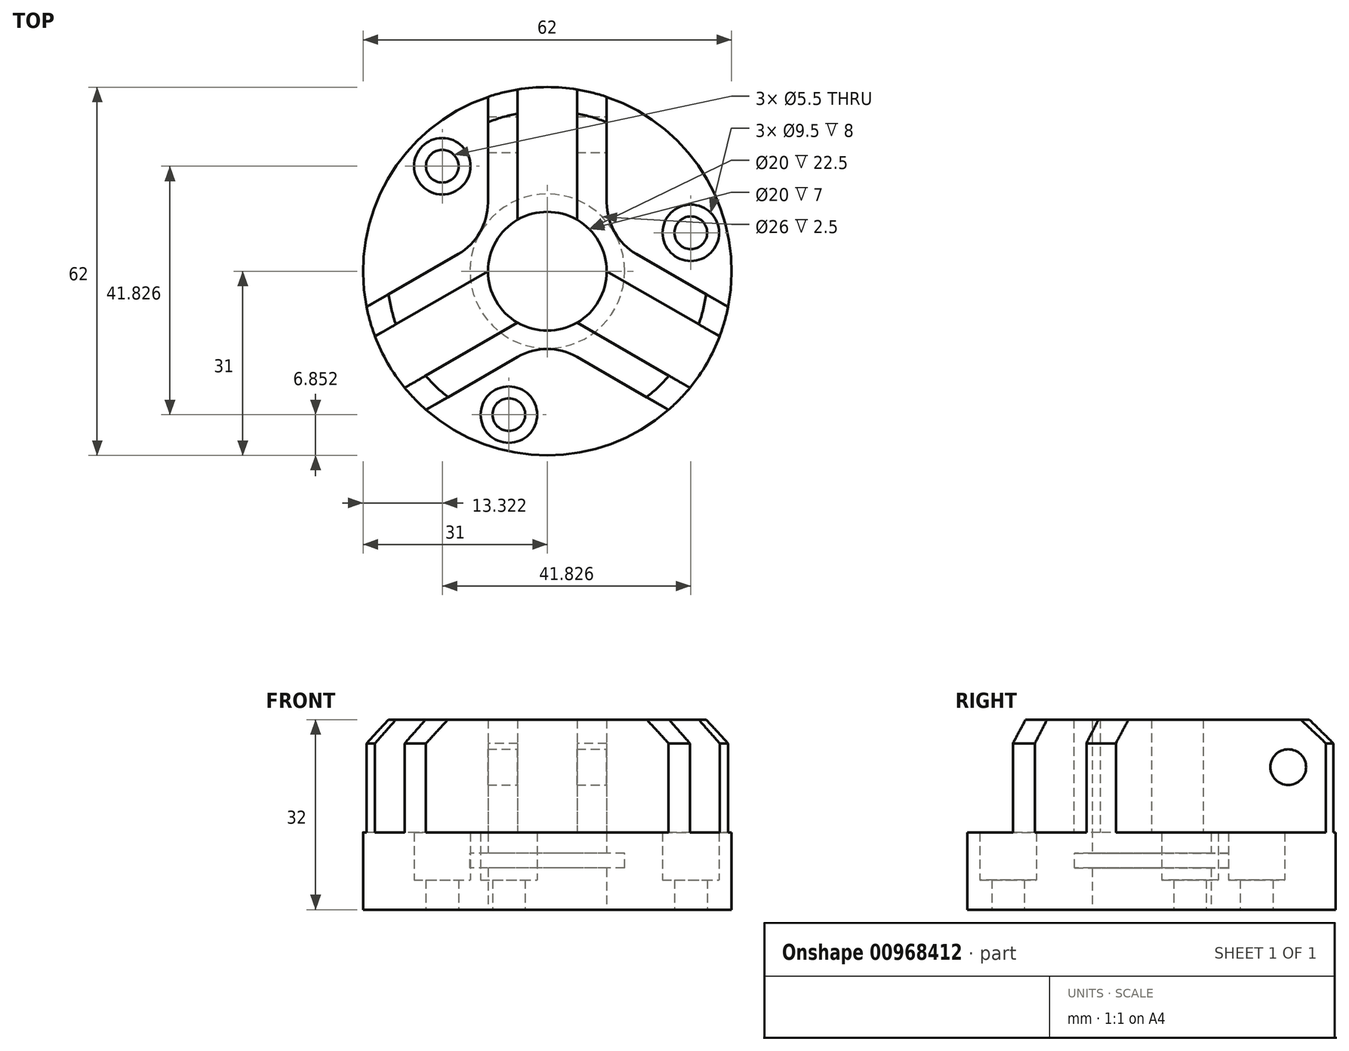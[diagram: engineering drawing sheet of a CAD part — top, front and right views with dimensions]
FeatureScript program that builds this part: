
annotation { "Feature Type Name" : "Feature", "Feature Type Description" : "" }
export const myFeature = defineFeature(function(context is Context, id is Id, definition is map)
    precondition{}
    {
        {
            var Q0;
            Q0=qCreatedBy(makeId("Top.planeOp"),FACE);
            cPlane(context, id + "F0", {"entities" : qUnion([Q0]), "cplaneType" : CPlaneType.OFFSET, "offset" : 13 * mm, "width" : 150 * mm, "height" : 150 * mm});
        }
        {
            var Q0;
            Q0=qCreatedBy(makeId("Top.planeOp"),FACE);
            cPlane(context, id + "F1", {"entities" : qUnion([Q0]), "cplaneType" : CPlaneType.OFFSET, "offset" : 32 * mm, "width" : 150 * mm, "height" : 150 * mm});
        }
        {
            var Q0;
            Q0=qCreatedBy(makeId("Top.planeOp"),FACE);
            var sketch = newSketch(context, id + "F2", { "sketchPlane" : qUnion([Q0])});
            skCircle(sketch, "E0", {"center": v(0, 0) * mm, "radius": 31 * mm});
            skCircle(sketch, "E1", {"center": v(0, 0) * mm, "radius": 10 * mm});
            skLineSegment(sketch, "E2", {"start": v(-5, 30.6) * mm, "end": v(-5, 8.66) * mm});
            skLineSegment(sketch, "E3", {"start": v(0, 0) * mm, "end": v(-26.85, -15.5) * mm, "construction": true});
            skLineSegment(sketch, "E4", {"start": v(0, 0) * mm, "end": v(26.85, -15.5) * mm, "construction": true});
            skLineSegment(sketch, "E5", {"start": v(-5, -8.66) * mm, "end": v(-24, -19.63) * mm});
            skLineSegment(sketch, "E6", {"start": v(-10, 0) * mm, "end": v(-29, -10.97) * mm});
            skLineSegment(sketch, "E7", {"start": v(5, 30.6) * mm, "end": v(5, 8.66) * mm});
            skLineSegment(sketch, "E8", {"start": v(-10, 29.34) * mm, "end": v(-10, 11.55) * mm});
            skLineSegment(sketch, "E9", {"start": v(-15, 2.89) * mm, "end": v(-30.41, -6.01) * mm});
            skPoint(sketch, "E10.visualSharp", {"position": v(-10, 5.77) * mm});
            skArc(sketch, "E10.filletArc", {"start": v(-15, 2.89) * mm, "mid": v(-11.34, 6.55) * mm, "end": v(-10, 11.55) * mm});
            skLineSegment(sketch, "E11.MirrorCS", {"start": v(10, 29.34) * mm, "end": v(10, 11.55) * mm});
            skArc(sketch, "E12.MirrorCS", {"start": v(15, 2.89) * mm, "mid": v(11.34, 6.55) * mm, "end": v(10, 11.55) * mm});
            skLineSegment(sketch, "E13.MirrorCS", {"start": v(15, 2.89) * mm, "end": v(30.41, -6.01) * mm});
            skLineSegment(sketch, "E14.MirrorCS", {"start": v(10, 0) * mm, "end": v(29, -10.97) * mm});
            skLineSegment(sketch, "E15.MirrorCS", {"start": v(5, -8.66) * mm, "end": v(24, -19.63) * mm});
            skLineSegment(sketch, "E16", {"start": v(-20.41, -23.33) * mm, "end": v(-5, -14.43) * mm});
            skLineSegment(sketch, "E17", {"start": v(5, -14.43) * mm, "end": v(20.41, -23.33) * mm});
            skPoint(sketch, "E18.visualSharp", {"position": v(0, -11.55) * mm});
            skArc(sketch, "E18.filletArc", {"start": v(5, -14.43) * mm, "mid": v(0, -13.1) * mm, "end": v(-5, -14.43) * mm});
            skLineSegment(sketch, "E19", {"start": v(0, 0) * mm, "end": v(-8.02, -29.94) * mm, "construction": true});
            skCircle(sketch, "E20", {"center": v(0, 0) * mm, "radius": 25 * mm, "construction": true});
            skLineSegment(sketch, "E21", {"start": v(0, 0) * mm, "end": v(-21.92, 21.92) * mm, "construction": true});
            skLineSegment(sketch, "E22", {"start": v(0, 0) * mm, "end": v(29.94, 8.02) * mm, "construction": true});
            skPoint(sketch, "E23", {"position": v(-17.68, 17.68) * mm});
            skPoint(sketch, "E24", {"position": v(24.15, 6.47) * mm});
            skPoint(sketch, "E25", {"position": v(-6.47, -24.15) * mm});
            skSolve(sketch);
        }
        {
            var Q0;
            Q0=qCreatedBy(makeId("Front.planeOp"),FACE);
            var sketch = newSketch(context, id + "F3", { "sketchPlane" : qUnion([Q0])});
            skLineSegment(sketch, "E26", {"start": v(20, 0) * mm, "end": v(10, 0) * mm});
            skLineSegment(sketch, "E27", {"start": v(10, 0) * mm, "end": v(10, 7) * mm});
            skLineSegment(sketch, "E28", {"start": v(10, 7) * mm, "end": v(13, 7) * mm});
            skLineSegment(sketch, "E29", {"start": v(13, 7) * mm, "end": v(13, 9.5) * mm});
            skLineSegment(sketch, "E30", {"start": v(13, 9.5) * mm, "end": v(10, 9.5) * mm});
            skLineSegment(sketch, "E31", {"start": v(10, 9.5) * mm, "end": v(10, 13) * mm});
            skLineSegment(sketch, "E32", {"start": v(10, 13) * mm, "end": v(31, 13) * mm});
            skLineSegment(sketch, "E33", {"start": v(31, 13) * mm, "end": v(31, 5) * mm});
            skLineSegment(sketch, "E34", {"start": v(31, 5) * mm, "end": v(17, 5) * mm});
            skLineSegment(sketch, "E35", {"start": v(17, 5) * mm, "end": v(17, 2) * mm});
            skLineSegment(sketch, "E36", {"start": v(17, 2) * mm, "end": v(20, 2) * mm});
            skLineSegment(sketch, "E37", {"start": v(20, 2) * mm, "end": v(20, 0) * mm});
            skLineSegment(sketch, "E38", {"start": v(31, 0) * mm, "end": v(20, 0) * mm, "construction": true});
            skLineSegment(sketch, "E39", {"start": v(0, 0) * mm, "end": v(0, 13) * mm, "construction": true});
            skLineSegment(sketch, "E40", {"start": v(31, 28) * mm, "end": v(27, 32) * mm});
            skLineSegment(sketch, "E41", {"start": v(27, 32) * mm, "end": v(31, 32) * mm});
            skLineSegment(sketch, "E42", {"start": v(31, 32) * mm, "end": v(31, 28) * mm});
            skLineSegment(sketch, "E43", {"start": v(10, 9.5) * mm, "end": v(10, 7) * mm});
            skSolve(sketch);
        }
        {
            var Q0;
            Q0=qCreatedBy(makeId("Right.planeOp"),FACE);
            var sketch = newSketch(context, id + "F4", { "sketchPlane" : qUnion([Q0])});
            skCircle(sketch, "E44", {"center": v(23, 24) * mm, "radius": 3 * mm});
            skSolve(sketch);
        }
        {
            var Q0;
            {var subQ0=sQuery(id+"F2.wireOp",EDGE,"E8");Q0=makeQuery(id+"F2.imprint","IMPRINT",FACE,{"disambiguationData":[TD([[makeQuery(id+"F2.imprint","IMPRINT",EDGE,{"derivedFrom":subQ0}),-1.0]])]});}
            var Q1;
            {var subQ0=sQuery(id+"F2.wireOp",EDGE,"E16");Q1=makeQuery(id+"F2.imprint","IMPRINT",FACE,{"disambiguationData":[TD([[makeQuery(id+"F2.imprint","IMPRINT",EDGE,{"derivedFrom":subQ0}),-1.0]])]});}
            var Q2;
            {var subQ0=sQuery(id+"F2.wireOp",EDGE,"E11.MirrorCS");Q2=makeQuery(id+"F2.imprint","IMPRINT",FACE,{"disambiguationData":[TD([[makeQuery(id+"F2.imprint","IMPRINT",EDGE,{"derivedFrom":subQ0}),1.0]])]});}
            var Q3;
            {var subQ0=sQuery(id+"F2.wireOp",EDGE,"E14.MirrorCS");Q3=makeQuery(id+"F2.imprint","IMPRINT",FACE,{"disambiguationData":[TD([[makeQuery(id+"F2.imprint","IMPRINT",EDGE,{"derivedFrom":subQ0}),-1.0]])]});}
            var Q4;
            {var subQ0=sQuery(id+"F2.wireOp",EDGE,"E2");Q4=makeQuery(id+"F2.imprint","IMPRINT",FACE,{"disambiguationData":[TD([[makeQuery(id+"F2.imprint","IMPRINT",EDGE,{"derivedFrom":subQ0}),1.0]])]});}
            var Q5;
            {var subQ0=sQuery(id+"F2.wireOp",EDGE,"E5");Q5=makeQuery(id+"F2.imprint","IMPRINT",FACE,{"disambiguationData":[TD([[makeQuery(id+"F2.imprint","IMPRINT",EDGE,{"derivedFrom":subQ0}),-1.0]])]});}
            var Q6;
            Q6=qCreatedBy(id+"F0.planeOp",FACE);
            extrude(context, id + "F5", {"entities" : qUnion([Q0, Q1, Q2, Q3, Q4, Q5]), "endBound" : BoundingType.UP_TO_SURFACE, "depth" : 25 * mm, "endBoundEntityFace" : qUnion([Q6]), "offsetDistance" : 25 * mm});
        }
        {
            var Q0;
            {var subQ0=sQuery(id+"F2.wireOp",EDGE,"E5");Q0=makeQuery(id+"F2.imprint","IMPRINT",FACE,{"disambiguationData":[TD([[makeQuery(id+"F2.imprint","IMPRINT",EDGE,{"derivedFrom":subQ0}),1.0]])]});}
            var Q1;
            {var subQ0=sQuery(id+"F2.wireOp",EDGE,"E7");Q1=makeQuery(id+"F2.imprint","IMPRINT",FACE,{"disambiguationData":[TD([[makeQuery(id+"F2.imprint","IMPRINT",EDGE,{"derivedFrom":subQ0}),1.0]])]});}
            var Q2;
            {var subQ0=sQuery(id+"F2.wireOp",EDGE,"E2");Q2=makeQuery(id+"F2.imprint","IMPRINT",FACE,{"disambiguationData":[TD([[makeQuery(id+"F2.imprint","IMPRINT",EDGE,{"derivedFrom":subQ0}),-1.0]])]});}
            var Q3;
            Q3=qCreatedBy(id+"F1.planeOp",FACE);
            extrude(context, id + "F6", {"entities" : qUnion([Q0, Q1, Q2]), "endBound" : BoundingType.UP_TO_SURFACE, "depth" : 25 * mm, "endBoundEntityFace" : qUnion([Q3]), "offsetDistance" : 25 * mm});
        }
        {
            var Q0;
            Q0=makeQuery(id+"F6.opExtrude","SWEPT_BODY",BODY,{"disambiguationData":[OSD([sQuery(id+"F2.wireOp",EDGE,"E0"),sQuery(id+"F2.wireOp",EDGE,"E1"),sQuery(id+"F2.wireOp",EDGE,"E5"),sQuery(id+"F2.wireOp",EDGE,"E15.MirrorCS"),sQuery(id+"F2.wireOp",EDGE,"E16"),sQuery(id+"F2.wireOp",EDGE,"E17"),sQuery(id+"F2.wireOp",EDGE,"E18.filletArc")])]});
            var Q1;
            Q1=makeQuery(id+"F6.opExtrude","SWEPT_BODY",BODY,{"disambiguationData":[OSD([sQuery(id+"F2.wireOp",EDGE,"E0"),sQuery(id+"F2.wireOp",EDGE,"E1"),sQuery(id+"F2.wireOp",EDGE,"E7"),sQuery(id+"F2.wireOp",EDGE,"E11.MirrorCS"),sQuery(id+"F2.wireOp",EDGE,"E12.MirrorCS"),sQuery(id+"F2.wireOp",EDGE,"E13.MirrorCS"),sQuery(id+"F2.wireOp",EDGE,"E14.MirrorCS")])]});
            var Q2;
            Q2=makeQuery(id+"F5.opExtrude","SWEPT_BODY",BODY,{"disambiguationData":[OSD([sQuery(id+"F2.wireOp",EDGE,"E0"),sQuery(id+"F2.wireOp",EDGE,"E11.MirrorCS"),sQuery(id+"F2.wireOp",EDGE,"E12.MirrorCS"),sQuery(id+"F2.wireOp",EDGE,"E13.MirrorCS")])]});
            var Q3;
            Q3=makeQuery(id+"F5.opExtrude","SWEPT_BODY",BODY,{"disambiguationData":[OSD([sQuery(id+"F2.wireOp",EDGE,"E0"),sQuery(id+"F2.wireOp",EDGE,"E1"),sQuery(id+"F2.wireOp",EDGE,"E14.MirrorCS"),sQuery(id+"F2.wireOp",EDGE,"E15.MirrorCS")])]});
            var Q4;
            Q4=makeQuery(id+"F5.opExtrude","SWEPT_BODY",BODY,{"disambiguationData":[OSD([sQuery(id+"F2.wireOp",EDGE,"E0"),sQuery(id+"F2.wireOp",EDGE,"E16"),sQuery(id+"F2.wireOp",EDGE,"E17"),sQuery(id+"F2.wireOp",EDGE,"E18.filletArc")])]});
            var Q5;
            Q5=makeQuery(id+"F5.opExtrude","SWEPT_BODY",BODY,{"disambiguationData":[OSD([sQuery(id+"F2.wireOp",EDGE,"E0"),sQuery(id+"F2.wireOp",EDGE,"E1"),sQuery(id+"F2.wireOp",EDGE,"E5"),sQuery(id+"F2.wireOp",EDGE,"E6")])]});
            var Q6;
            Q6=makeQuery(id+"F5.opExtrude","SWEPT_BODY",BODY,{"disambiguationData":[OSD([sQuery(id+"F2.wireOp",EDGE,"E0"),sQuery(id+"F2.wireOp",EDGE,"E1"),sQuery(id+"F2.wireOp",EDGE,"E2"),sQuery(id+"F2.wireOp",EDGE,"E7")])]});
            var Q7;
            Q7=makeQuery(id+"F6.opExtrude","SWEPT_BODY",BODY,{"disambiguationData":[OSD([sQuery(id+"F2.wireOp",EDGE,"E0"),sQuery(id+"F2.wireOp",EDGE,"E1"),sQuery(id+"F2.wireOp",EDGE,"E2"),sQuery(id+"F2.wireOp",EDGE,"E6"),sQuery(id+"F2.wireOp",EDGE,"E8"),sQuery(id+"F2.wireOp",EDGE,"E9"),sQuery(id+"F2.wireOp",EDGE,"E10.filletArc")])]});
            var Q8;
            Q8=makeQuery(id+"F5.opExtrude","SWEPT_BODY",BODY,{"disambiguationData":[OSD([sQuery(id+"F2.wireOp",EDGE,"E0"),sQuery(id+"F2.wireOp",EDGE,"E8"),sQuery(id+"F2.wireOp",EDGE,"E9"),sQuery(id+"F2.wireOp",EDGE,"E10.filletArc")])]});
            booleanBodies(context, id + "F7", {"operationType" : BooleanOperationType.UNION, "tools" : qUnion([Q0, Q1, Q2, Q3, Q4, Q5, Q6, Q7, Q8])});
        }
        {
            var Q0;
            Q0=makeQuery(id+"F3.imprint","IMPRINT",FACE,{"disambiguationData":[TD([[makeQuery(id+"F3.imprint","IMPRINT",EDGE,{"derivedFrom":sQuery(id+"F3.wireOp",EDGE,"E28")}),1.0]])]});
            var Q1;
            Q1=sQuery(id+"F3.wireOp",EDGE,"E39");
            revolve(context, id + "F8", {"operationType" : NewBodyOperationType.REMOVE, "surfaceOperationType" : NewSurfaceOperationType.NEW, "entities" : qUnion([Q0]), "axis" : qUnion([Q1]), "revolveType" : RevolveType.FULL, "oppositeDirection" : true});
        }
        {
            var Q0;
            Q0=makeQuery(id+"F3.imprint","IMPRINT",FACE,{"disambiguationData":[TD([[makeQuery(id+"F3.imprint","IMPRINT",EDGE,{"derivedFrom":sQuery(id+"F3.wireOp",EDGE,"E40")}),-1.0]])]});
            var Q1;
            Q1=sQuery(id+"F3.wireOp",EDGE,"E39");
            revolve(context, id + "F9", {"operationType" : NewBodyOperationType.REMOVE, "surfaceOperationType" : NewSurfaceOperationType.NEW, "entities" : qUnion([Q0]), "axis" : qUnion([Q1]), "revolveType" : RevolveType.FULL, "oppositeDirection" : true});
        }
        {
            var Q0;
            Q0=makeQuery(id+"F4.imprint","IMPRINT",FACE,{"disambiguationData":[TD([[makeQuery(id+"F4.imprint","IMPRINT",EDGE,{"derivedFrom":sQuery(id+"F4.wireOp",EDGE,"E44")}),1.0]])]});
            extrude(context, id + "F10", {"entities" : qUnion([Q0]), "operationType" : NewBodyOperationType.REMOVE, "oppositeDirection" : true, "depth" : 25 * mm, "offsetDistance" : 25 * mm, "symmetric" : true});
        }
        {
            var Q0;
            Q0=makeQuery(id+"F5.opExtrude","CAP_FACE",FACE,{"disambiguationData":[OSD([sQuery(id+"F2.wireOp",EDGE,"E0"),sQuery(id+"F2.wireOp",EDGE,"E16"),sQuery(id+"F2.wireOp",EDGE,"E17"),sQuery(id+"F2.wireOp",EDGE,"E18.filletArc")])],"isStart":false});
            var sketch = newSketch(context, id + "F11", { "sketchPlane" : qUnion([Q0])});
            skPoint(sketch, "E45.0", {"position": v(-6.47, -24.15) * mm});
            skPoint(sketch, "E45.1", {"position": v(24.15, 6.47) * mm});
            skPoint(sketch, "E45.2", {"position": v(-17.68, 17.68) * mm});
            skSolve(sketch);
        }
        {
            var Q0;
            Q0=sQuery(id+"F11.wireOp",VERTEX,"E45.0");
            var Q1;
            Q1=sQuery(id+"F11.wireOp",VERTEX,"E45.1");
            var Q2;
            Q2=sQuery(id+"F11.wireOp",VERTEX,"E45.2");
            var Q3;
            Q3=makeQuery(id+"F6.opExtrude","SWEPT_BODY",BODY,{"disambiguationData":[OSD([sQuery(id+"F2.wireOp",EDGE,"E0"),sQuery(id+"F2.wireOp",EDGE,"E1"),sQuery(id+"F2.wireOp",EDGE,"E5"),sQuery(id+"F2.wireOp",EDGE,"E15.MirrorCS"),sQuery(id+"F2.wireOp",EDGE,"E16"),sQuery(id+"F2.wireOp",EDGE,"E17"),sQuery(id+"F2.wireOp",EDGE,"E18.filletArc")])]});
            hole(context, id + "F12", {"style" : HoleStyle.C_BORE, "endStyle" : HoleEndStyle.THROUGH, "holeDiameter" : 5.5 * mm, "cBoreDiameter" : 9.5 * mm, "cBoreDepth" : 8 * mm, "majorDiameter" : 5 * mm, "isTappedThrough" : true, "tappedDepth" : 25 * mm, "tapClearance" : 0, "startFromSketch" : true, "locations" : qUnion([Q0, Q1, Q2]), "scope" : qUnion([Q3])});
        }
    });
